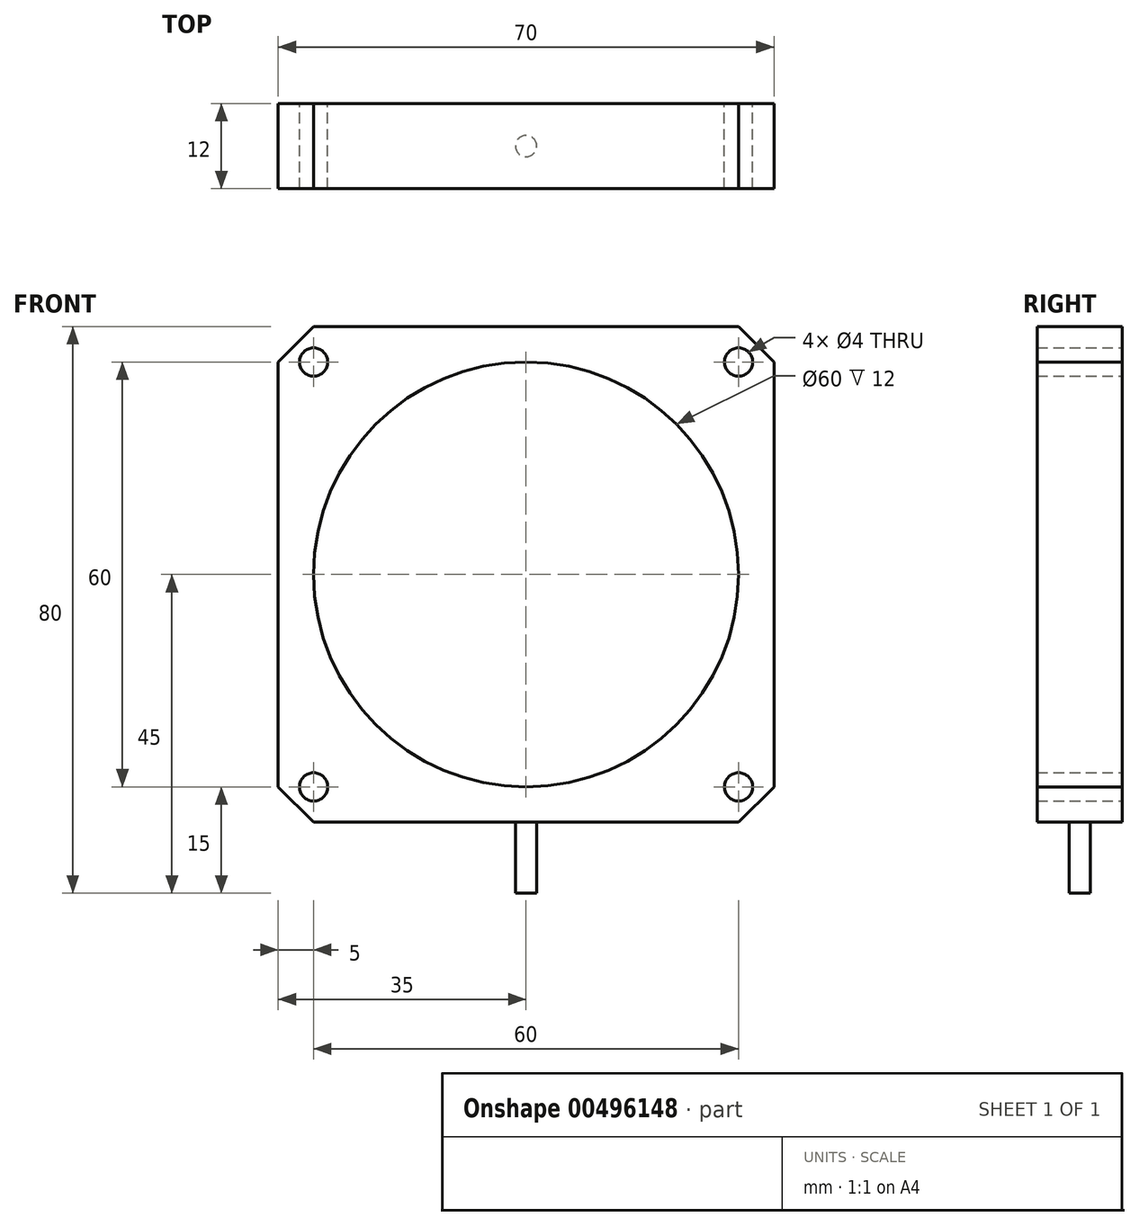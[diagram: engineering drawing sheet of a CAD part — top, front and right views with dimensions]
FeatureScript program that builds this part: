
annotation { "Feature Type Name" : "Feature", "Feature Type Description" : "" }
export const myFeature = defineFeature(function(context is Context, id is Id, definition is map)
    precondition{}
    {
        {
            var Q0;
            Q0=qCreatedBy(makeId("Front.planeOp"),FACE);
            var sketch = newSketch(context, id + "F0", { "sketchPlane" : qUnion([Q0])});
            skLineSegment(sketch, "E0.bottom", {"start": v(35, 35) * mm, "end": v(-35, 35) * mm});
            skLineSegment(sketch, "E0.top", {"start": v(35, -35) * mm, "end": v(-35, -35) * mm});
            skLineSegment(sketch, "E0.left", {"start": v(35, 35) * mm, "end": v(35, -35) * mm});
            skLineSegment(sketch, "E0.right", {"start": v(-35, 35) * mm, "end": v(-35, -35) * mm});
            skPoint(sketch, "E0.middle", {"position": v(0, 0) * mm});
            skCircle(sketch, "E1", {"center": v(0, 0) * mm, "radius": 30 * mm});
            skPoint(sketch, "E2", {"position": v(-30, 30) * mm});
            skPoint(sketch, "E3", {"position": v(30, 30) * mm});
            skPoint(sketch, "E4", {"position": v(30, -30) * mm});
            skPoint(sketch, "E5", {"position": v(-30, -30) * mm});
            skCircle(sketch, "E6", {"center": v(-30, 30) * mm, "radius": 2 * mm});
            skCircle(sketch, "E7", {"center": v(30, 30) * mm, "radius": 2 * mm});
            skCircle(sketch, "E8", {"center": v(30, -30) * mm, "radius": 2 * mm});
            skCircle(sketch, "E9", {"center": v(-30, -30) * mm, "radius": 2 * mm});
            skSolve(sketch);
        }
        {
            var Q0;
            Q0=qSketchRegion(id+"F0",true);
            extrude(context, id + "F1", {"entities" : qUnion([Q0]), "depth" : 12 * mm});
        }
        {
            var Q0;
            Q0=makeQuery(id+"F1.opExtrude","SWEPT_EDGE",EDGE,{"disambiguationData":[OSD([sQuery(id+"F0.wireOp",EDGE,"E0.bottom"),sQuery(id+"F0.wireOp",EDGE,"E0.right")])]});
            var Q1;
            Q1=makeQuery(id+"F1.opExtrude","SWEPT_EDGE",EDGE,{"disambiguationData":[OSD([sQuery(id+"F0.wireOp",EDGE,"E0.bottom"),sQuery(id+"F0.wireOp",EDGE,"E0.left")])]});
            var Q2;
            Q2=makeQuery(id+"F1.opExtrude","SWEPT_EDGE",EDGE,{"disambiguationData":[OSD([sQuery(id+"F0.wireOp",EDGE,"E0.top"),sQuery(id+"F0.wireOp",EDGE,"E0.left")])]});
            var Q3;
            Q3=makeQuery(id+"F1.opExtrude","SWEPT_EDGE",EDGE,{"disambiguationData":[OSD([sQuery(id+"F0.wireOp",EDGE,"E0.top"),sQuery(id+"F0.wireOp",EDGE,"E0.right")])]});
            chamfer(context, id + "F2", {"entities" : qUnion([Q0, Q1, Q2, Q3]), "width" : 5 * mm, "tangentPropagation" : true});
        }
        {
            var Q0;
            Q0=makeQuery(id+"F1.opExtrude","SWEPT_FACE",FACE,{"disambiguationData":[OSD([sQuery(id+"F0.wireOp",EDGE,"E0.top")])]});
            var sketch = newSketch(context, id + "F3", { "sketchPlane" : qUnion([Q0])});
            skCircle(sketch, "E10", {"center": v(0, 6) * mm, "radius": 1.5 * mm});
            skSolve(sketch);
        }
        {
            var Q0;
            Q0=qSketchRegion(id+"F3",true);
            extrude(context, id + "F4", {"entities" : qUnion([Q0]), "operationType" : NewBodyOperationType.ADD, "depth" : 10 * mm});
        }
    });
